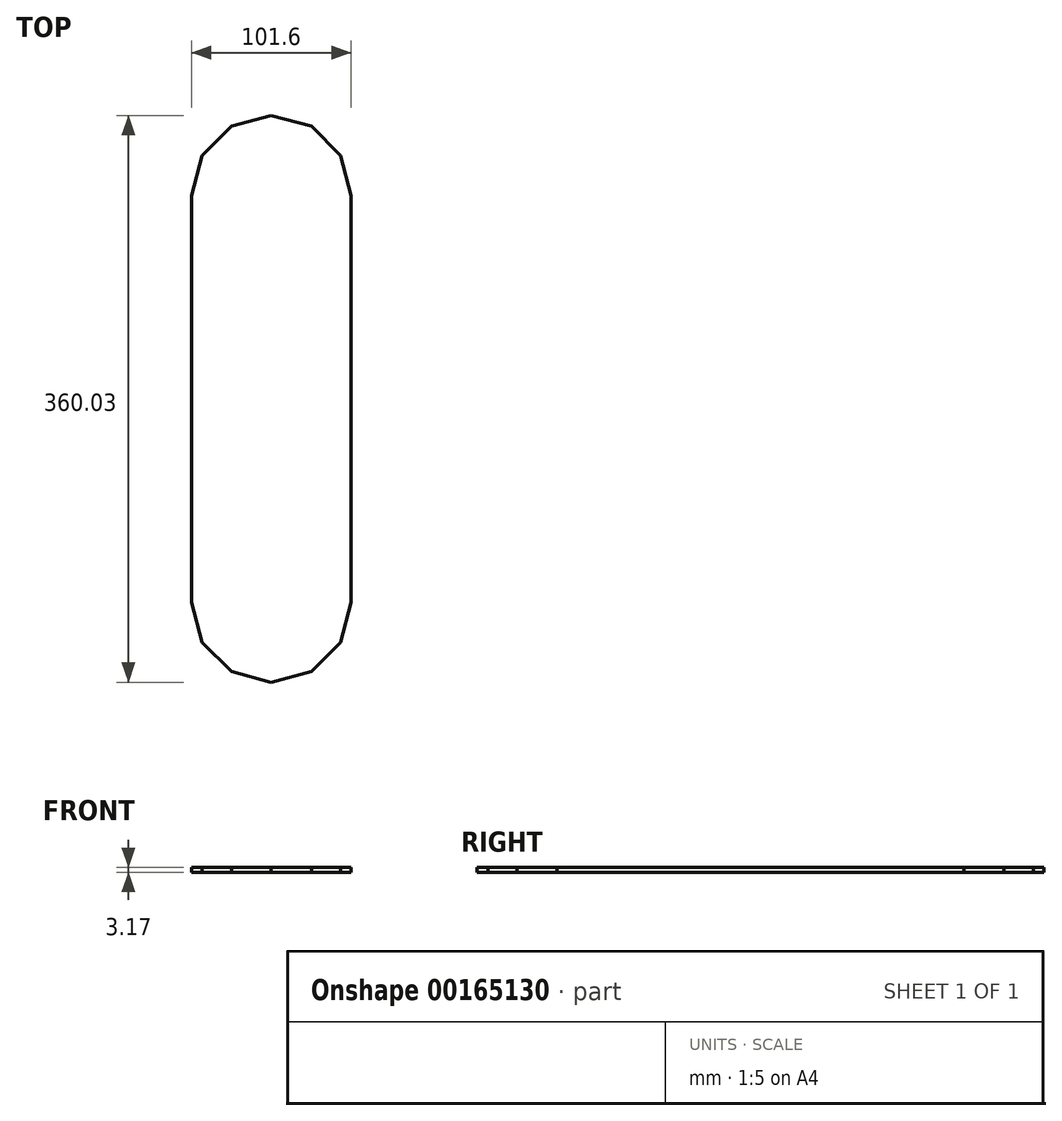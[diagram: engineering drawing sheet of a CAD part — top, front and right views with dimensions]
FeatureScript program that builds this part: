
annotation { "Feature Type Name" : "Feature", "Feature Type Description" : "" }
export const myFeature = defineFeature(function(context is Context, id is Id, definition is map)
    precondition{}
    {
        {
            var Q0;
            Q0=qCreatedBy(makeId("Top.planeOp"),FACE);
            var sketch = newSketch(context, id + "F0", { "sketchPlane" : qUnion([Q0])});
            skLineSegment(sketch, "E0", {"start": v(50.8, 0) * mm, "end": v(101.6, 0) * mm, "construction": true});
            skLineSegment(sketch, "E1", {"start": v(50.8, 0) * mm, "end": v(94.8, 25.4) * mm, "construction": true});
            skLineSegment(sketch, "E2", {"start": v(50.8, 0) * mm, "end": v(76.2, 44) * mm, "construction": true});
            skLineSegment(sketch, "E3", {"start": v(50.8, 0) * mm, "end": v(50.8, 50.8) * mm, "construction": true});
            skLineSegment(sketch, "E4", {"start": v(101.6, 0) * mm, "end": v(94.8, 25.4) * mm});
            skLineSegment(sketch, "E5", {"start": v(94.8, 25.4) * mm, "end": v(76.2, 44) * mm});
            skLineSegment(sketch, "E6", {"start": v(76.2, 44) * mm, "end": v(50.8, 50.8) * mm});
            skLineSegment(sketch, "E7", {"start": v(101.6, 0) * mm, "end": v(101.6, -258.43) * mm});
            skLineSegment(sketch, "E8", {"start": v(101.6, -258.43) * mm, "end": v(50.8, -258.43) * mm, "construction": true});
            skLineSegment(sketch, "E9", {"start": v(50.8, -258.43) * mm, "end": v(94.8, -283.83) * mm, "construction": true});
            skLineSegment(sketch, "E10", {"start": v(50.8, 0) * mm, "end": v(25.4, 44) * mm, "construction": true});
            skLineSegment(sketch, "E11", {"start": v(50.8, 0) * mm, "end": v(6.8, 25.4) * mm, "construction": true});
            skLineSegment(sketch, "E12", {"start": v(50.8, 0) * mm, "end": v(0, 0) * mm, "construction": true});
            skLineSegment(sketch, "E13", {"start": v(50.8, -258.43) * mm, "end": v(0, -258.43) * mm, "construction": true});
            skLineSegment(sketch, "E14", {"start": v(50.8, 50.8) * mm, "end": v(25.4, 44) * mm});
            skLineSegment(sketch, "E15", {"start": v(25.4, 44) * mm, "end": v(6.8, 25.4) * mm});
            skLineSegment(sketch, "E16", {"start": v(6.8, 25.4) * mm, "end": v(0, 0) * mm});
            skLineSegment(sketch, "E17", {"start": v(0, 0) * mm, "end": v(0, -258.43) * mm});
            skLineSegment(sketch, "E18", {"start": v(50.8, -258.43) * mm, "end": v(76.2, -302.43) * mm, "construction": true});
            skLineSegment(sketch, "E19", {"start": v(50.8, -258.43) * mm, "end": v(50.8, -309.23) * mm, "construction": true});
            skLineSegment(sketch, "E20", {"start": v(50.8, -258.43) * mm, "end": v(25.4, -302.43) * mm, "construction": true});
            skLineSegment(sketch, "E21", {"start": v(50.8, -258.43) * mm, "end": v(6.8, -283.83) * mm, "construction": true});
            skLineSegment(sketch, "E22", {"start": v(0, -258.43) * mm, "end": v(6.8, -283.83) * mm});
            skLineSegment(sketch, "E23", {"start": v(6.8, -283.83) * mm, "end": v(25.4, -302.43) * mm});
            skLineSegment(sketch, "E24", {"start": v(25.4, -302.43) * mm, "end": v(50.8, -309.23) * mm});
            skLineSegment(sketch, "E25", {"start": v(50.8, -309.23) * mm, "end": v(76.2, -302.43) * mm});
            skLineSegment(sketch, "E26", {"start": v(76.2, -302.43) * mm, "end": v(94.8, -283.83) * mm});
            skLineSegment(sketch, "E27", {"start": v(94.8, -283.83) * mm, "end": v(101.6, -258.43) * mm});
            skLineSegment(sketch, "E28", {"start": v(50.8, 0) * mm, "end": v(50.8, -129.22) * mm, "construction": true});
            skLineSegment(sketch, "E29", {"start": v(50.8, -129.22) * mm, "end": v(50.8, -258.43) * mm, "construction": true});
            skSolve(sketch);
        }
        {
            var Q0;
            Q0=qSketchRegion(id+"F0",true);
            extrude(context, id + "F1", {"entities" : qUnion([Q0]), "depth" : 3.17 * mm});
        }
    });
